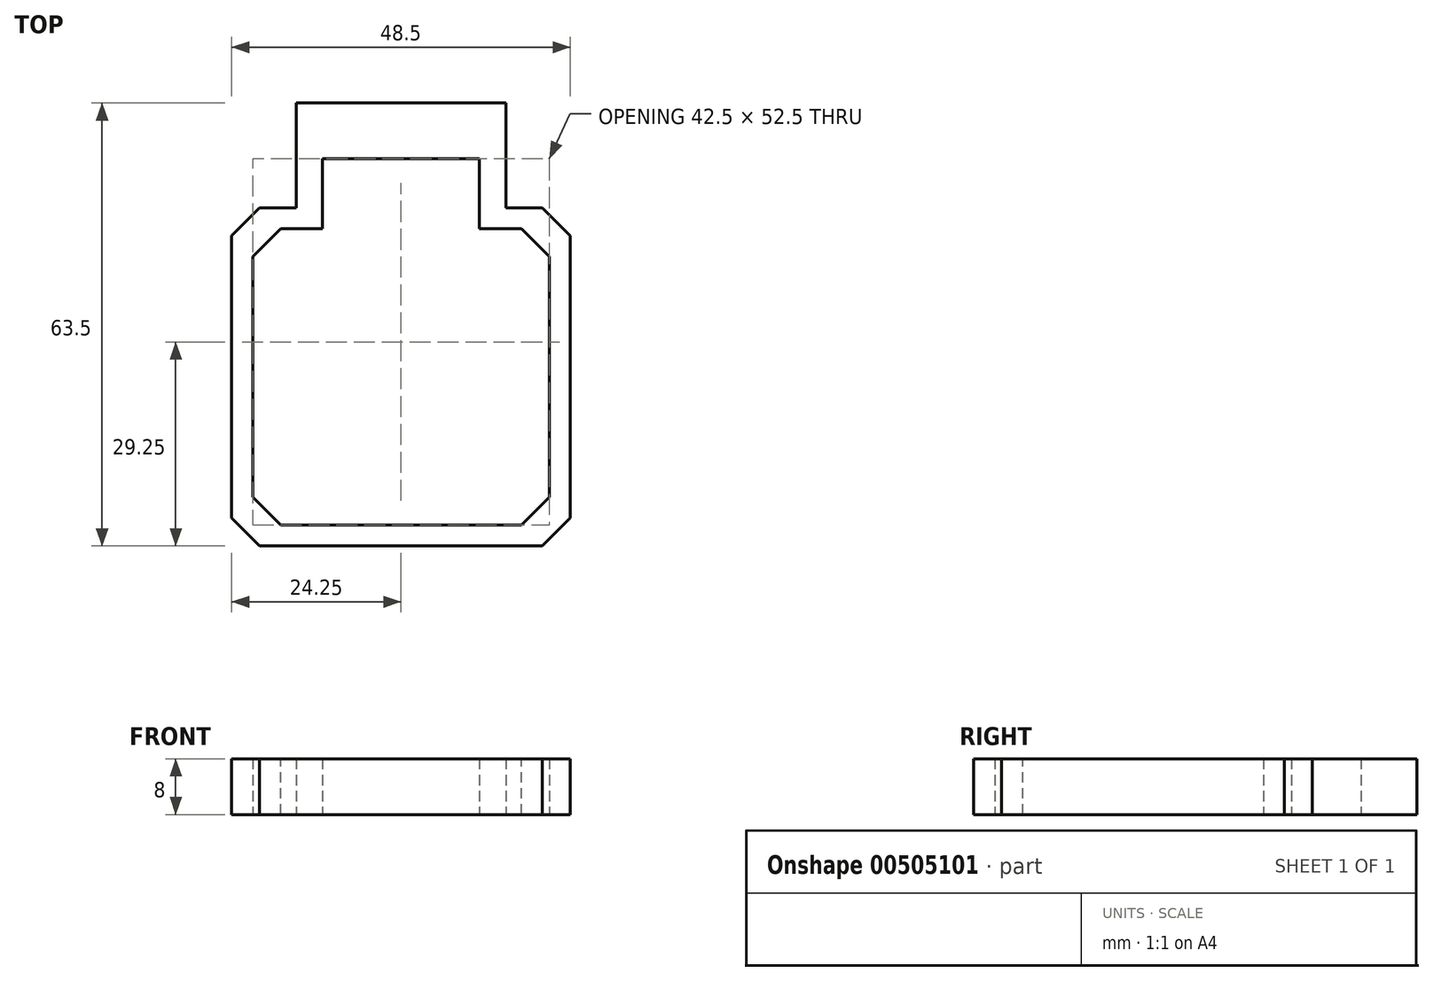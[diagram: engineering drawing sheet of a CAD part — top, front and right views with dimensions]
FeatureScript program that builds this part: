
annotation { "Feature Type Name" : "Feature", "Feature Type Description" : "" }
export const myFeature = defineFeature(function(context is Context, id is Id, definition is map)
    precondition{}
    {
        {
            var Q0;
            Q0=qCreatedBy(makeId("Top.planeOp"),FACE);
            var sketch = newSketch(context, id + "F0", { "sketchPlane" : qUnion([Q0])});
            skLineSegment(sketch, "E0.bottom", {"start": v(21.25, -21.25) * mm, "end": v(-21.25, -21.25) * mm});
            skLineSegment(sketch, "E0.left", {"start": v(21.25, -21.25) * mm, "end": v(21.25, 21.25) * mm});
            skLineSegment(sketch, "E0.right", {"start": v(-21.25, -21.25) * mm, "end": v(-21.25, 21.25) * mm});
            skPoint(sketch, "E0.middle", {"position": v(0, 0) * mm});
            skLineSegment(sketch, "E1", {"start": v(-21.25, 21.25) * mm, "end": v(-11.25, 21.25) * mm});
            skLineSegment(sketch, "E2", {"start": v(21.25, 21.25) * mm, "end": v(11.25, 21.25) * mm});
            skLineSegment(sketch, "E3.0", {"start": v(-24.25, 24.25) * mm, "end": v(-11.25, 24.25) * mm});
            skLineSegment(sketch, "E3.1", {"start": v(24.25, 24.25) * mm, "end": v(11.25, 24.25) * mm});
            skLineSegment(sketch, "E3.2", {"start": v(24.25, -24.25) * mm, "end": v(24.25, 24.25) * mm});
            skLineSegment(sketch, "E3.3", {"start": v(24.25, -24.25) * mm, "end": v(-24.25, -24.25) * mm});
            skLineSegment(sketch, "E3.4", {"start": v(-24.25, -24.25) * mm, "end": v(-24.25, 24.25) * mm});
            skLineSegment(sketch, "E4", {"start": v(-11.25, 24.25) * mm, "end": v(-11.25, 21.25) * mm});
            skLineSegment(sketch, "E5", {"start": v(11.25, 24.25) * mm, "end": v(11.25, 21.25) * mm});
            skSolve(sketch);
        }
        {
            var Q0;
            Q0 = qSketchRegion(id + "F0", true);
            extrude(context, id + "F1", {"entities" : qUnion([Q0]), "depth" : 8 * mm});
        }
        {
            var Q0;
            Q0=makeQuery(id+"F1.opExtrude","SWEPT_EDGE",EDGE,{"disambiguationData":[OSD([sQuery(id+"F0.wireOp",EDGE,"E0.right"),sQuery(id+"F0.wireOp",EDGE,"E1")])]});
            var Q1;
            Q1=makeQuery(id+"F1.opExtrude","SWEPT_EDGE",EDGE,{"disambiguationData":[OSD([sQuery(id+"F0.wireOp",EDGE,"E0.bottom"),sQuery(id+"F0.wireOp",EDGE,"E0.right")])]});
            var Q2;
            Q2=makeQuery(id+"F1.opExtrude","SWEPT_EDGE",EDGE,{"disambiguationData":[OSD([sQuery(id+"F0.wireOp",EDGE,"E0.bottom"),sQuery(id+"F0.wireOp",EDGE,"E0.left")])]});
            var Q3;
            Q3=makeQuery(id+"F1.opExtrude","SWEPT_EDGE",EDGE,{"disambiguationData":[OSD([sQuery(id+"F0.wireOp",EDGE,"E3.3"),sQuery(id+"F0.wireOp",EDGE,"E3.4")])]});
            var Q4;
            Q4=makeQuery(id+"F1.opExtrude","SWEPT_EDGE",EDGE,{"disambiguationData":[OSD([sQuery(id+"F0.wireOp",EDGE,"E3.0"),sQuery(id+"F0.wireOp",EDGE,"E3.4")])]});
            var Q5;
            Q5=makeQuery(id+"F1.opExtrude","SWEPT_EDGE",EDGE,{"disambiguationData":[OSD([sQuery(id+"F0.wireOp",EDGE,"E3.1"),sQuery(id+"F0.wireOp",EDGE,"E3.2")])]});
            var Q6;
            Q6=makeQuery(id+"F1.opExtrude","SWEPT_EDGE",EDGE,{"disambiguationData":[OSD([sQuery(id+"F0.wireOp",EDGE,"E0.left"),sQuery(id+"F0.wireOp",EDGE,"E2")])]});
            var Q7;
            Q7=makeQuery(id+"F1.opExtrude","SWEPT_EDGE",EDGE,{"disambiguationData":[OSD([sQuery(id+"F0.wireOp",EDGE,"E3.2"),sQuery(id+"F0.wireOp",EDGE,"E3.3")])]});
            chamfer(context, id + "F2", {"entities" : qUnion([Q0, Q1, Q2, Q3, Q4, Q5, Q6, Q7]), "width" : 4 * mm, "tangentPropagation" : true});
        }
        {
            var Q0;
            Q0=makeQuery(id+"F1.opExtrude","CAP_FACE",FACE,{"disambiguationData":[OSD([sQuery(id+"F0.wireOp",EDGE,"E0.bottom"),sQuery(id+"F0.wireOp",EDGE,"E0.left"),sQuery(id+"F0.wireOp",EDGE,"E0.right"),sQuery(id+"F0.wireOp",EDGE,"E1"),sQuery(id+"F0.wireOp",EDGE,"E2"),sQuery(id+"F0.wireOp",EDGE,"E3.0"),sQuery(id+"F0.wireOp",EDGE,"E3.1"),sQuery(id+"F0.wireOp",EDGE,"E3.2"),sQuery(id+"F0.wireOp",EDGE,"E3.3"),sQuery(id+"F0.wireOp",EDGE,"E3.4"),sQuery(id+"F0.wireOp",EDGE,"E4"),sQuery(id+"F0.wireOp",EDGE,"E5")])],"isStart":true});
            var sketch = newSketch(context, id + "F3", { "sketchPlane" : qUnion([Q0])});
            skPoint(sketch, "E6.0", {"position": v(-11.25, -24.25) * mm});
            skPoint(sketch, "E7.0", {"position": v(11.25, -24.25) * mm});
            skLineSegment(sketch, "E8.bottom", {"start": v(-11.25, -24.25) * mm, "end": v(-15.02, -24.25) * mm});
            skLineSegment(sketch, "E8.top", {"start": v(-11.25, -39.25) * mm, "end": v(-15.02, -39.25) * mm});
            skLineSegment(sketch, "E8.left", {"start": v(-11.25, -24.25) * mm, "end": v(-11.25, -39.25) * mm});
            skLineSegment(sketch, "E8.right", {"start": v(-15.02, -24.25) * mm, "end": v(-15.02, -39.25) * mm});
            skLineSegment(sketch, "E9.bottom", {"start": v(-11.25, -39.25) * mm, "end": v(0, -39.25) * mm});
            skLineSegment(sketch, "E9.top", {"start": v(-11.25, -31.25) * mm, "end": v(0, -31.25) * mm});
            skLineSegment(sketch, "E9.left", {"start": v(-11.25, -39.25) * mm, "end": v(-11.25, -31.25) * mm});
            skLineSegment(sketch, "E9.right", {"start": v(0, -39.25) * mm, "end": v(0, -31.25) * mm});
            skLineSegment(sketch, "E10.MirrorCS", {"start": v(11.25, -39.25) * mm, "end": v(0, -39.25) * mm});
            skLineSegment(sketch, "E11.MirrorCS", {"start": v(11.25, -39.25) * mm, "end": v(11.25, -31.25) * mm});
            skLineSegment(sketch, "E12.MirrorCS", {"start": v(11.25, -31.25) * mm, "end": v(0, -31.25) * mm});
            skLineSegment(sketch, "E13.MirrorCS", {"start": v(15.02, -24.25) * mm, "end": v(15.02, -39.25) * mm});
            skLineSegment(sketch, "E14.MirrorCS", {"start": v(11.25, -39.25) * mm, "end": v(15.02, -39.25) * mm});
            skLineSegment(sketch, "E15.MirrorCS", {"start": v(11.25, -24.25) * mm, "end": v(15.02, -24.25) * mm});
            skLineSegment(sketch, "E16.MirrorCS", {"start": v(11.25, -24.25) * mm, "end": v(11.25, -39.25) * mm});
            skSolve(sketch);
        }
        {
            var Q0;
            Q0 = qSketchRegion(id + "F3", true);
            extrude(context, id + "F4", {"entities" : qUnion([Q0]), "operationType" : NewBodyOperationType.ADD, "oppositeDirection" : true, "depth" : 8 * mm});
        }
    });
